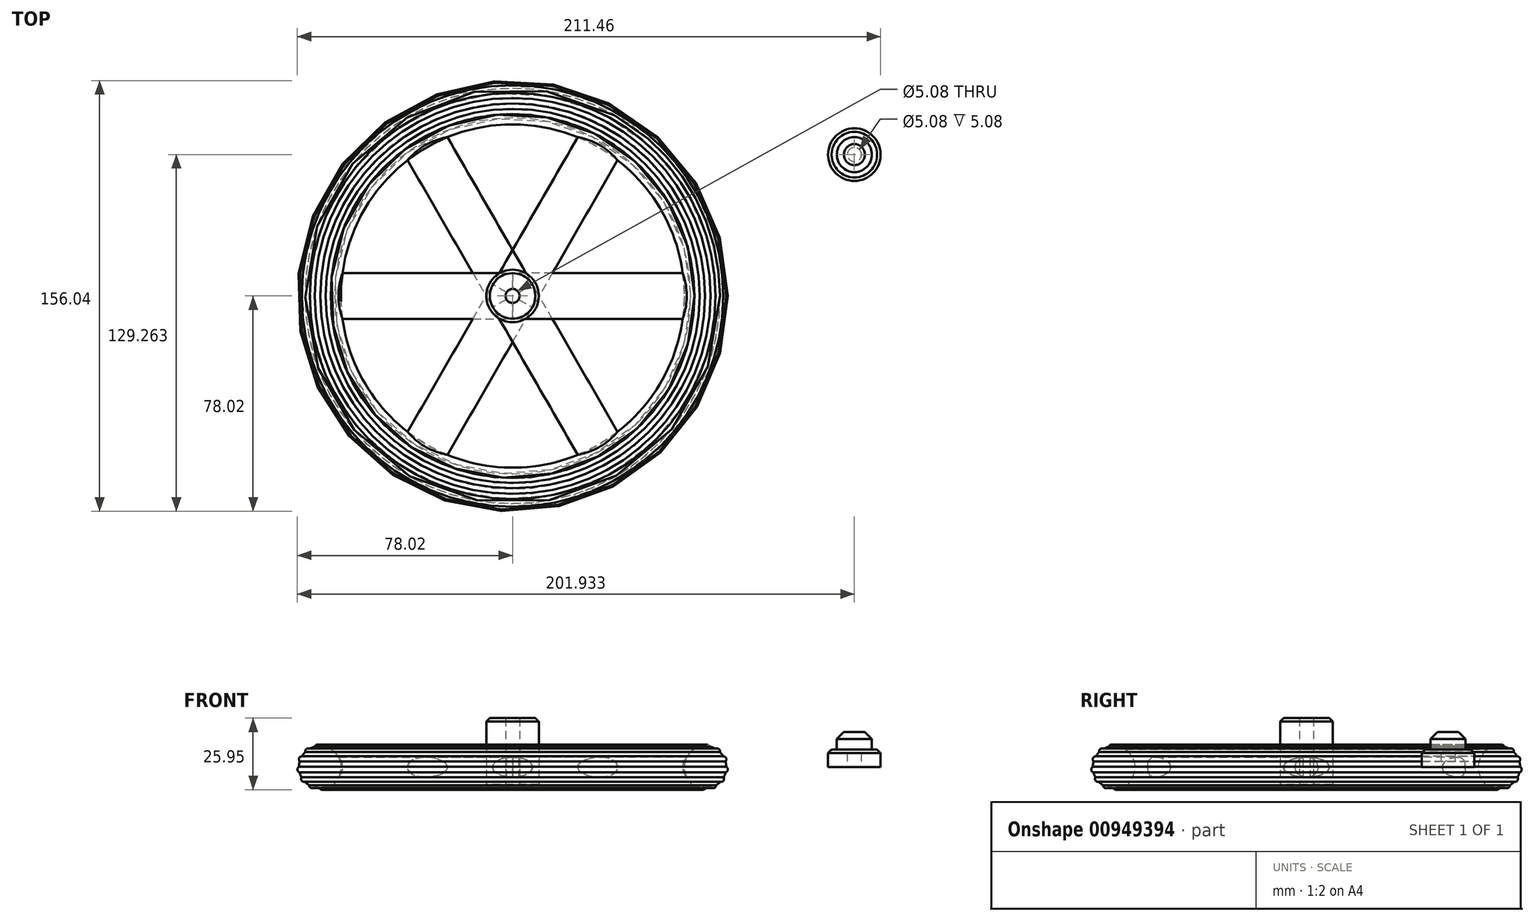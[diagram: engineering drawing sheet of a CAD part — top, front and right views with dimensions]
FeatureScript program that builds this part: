
annotation { "Feature Type Name" : "Feature", "Feature Type Description" : "" }
export const myFeature = defineFeature(function(context is Context, id is Id, definition is map)
    precondition{}
    {
        {
            var Q0;
            Q0=qCreatedBy(makeId("Front.planeOp"),FACE);
            var sketch = newSketch(context, id + "F0", { "sketchPlane" : qUnion([Q0])});
            skArc(sketch, "E0", {"start": v(-71.73, 7.38) * mm, "mid": v(-72.66, 7.08) * mm, "end": v(-73.55, 6.66) * mm});
            skArc(sketch, "E1", {"start": v(-69.72, 7.62) * mm, "mid": v(-70.8, 8.16) * mm, "end": v(-71.73, 7.38) * mm});
            skArc(sketch, "E2.1.1", {"start": v(-73.55, 6.66) * mm, "mid": v(-74.76, 6.6) * mm, "end": v(-75.17, 5.45) * mm});
            skArc(sketch, "E2.2.1", {"start": v(-76.38, 3.92) * mm, "mid": v(-77.4, 3.26) * mm, "end": v(-77.19, 2.06) * mm});
            skArc(sketch, "E2.3.1", {"start": v(-77.47, 0.13) * mm, "mid": v(-78.01, -0.95) * mm, "end": v(-77.23, -1.88) * mm});
            skArc(sketch, "E2.4.1", {"start": v(-76.51, -3.7) * mm, "mid": v(-76.44, -4.9) * mm, "end": v(-75.3, -5.32) * mm});
            skArc(sketch, "E2.5.1", {"start": v(-73.77, -6.53) * mm, "mid": v(-73.1, -7.55) * mm, "end": v(-71.91, -7.34) * mm});
            skArc(sketch, "E2.6.1", {"start": v(-69.98, -7.62) * mm, "mid": v(-68.9, -8.16) * mm, "end": v(-67.97, -7.38) * mm});
            skArc(sketch, "E2.7.1", {"start": v(-66.15, -6.66) * mm, "mid": v(-64.94, -6.6) * mm, "end": v(-64.53, -5.45) * mm});
            skArc(sketch, "E2.11.1", {"start": v(-65.93, 6.53) * mm, "mid": v(-66.6, 7.55) * mm, "end": v(-67.79, 7.34) * mm});
            skArc(sketch, "E3.trimOffspring", {"start": v(-75.17, 5.45) * mm, "mid": v(-75.83, 4.73) * mm, "end": v(-76.38, 3.92) * mm});
            skArc(sketch, "E4.trimOffspring", {"start": v(-67.79, 7.34) * mm, "mid": v(-68.75, 7.54) * mm, "end": v(-69.72, 7.62) * mm});
            skArc(sketch, "E5.trimOffspring", {"start": v(-62.92, 3.16) * mm, "mid": v(-64.17, 5.07) * mm, "end": v(-65.93, 6.53) * mm});
            skArc(sketch, "E6.trimOffspring", {"start": v(-62.36, -1.42) * mm, "mid": v(-62.28, 0.9) * mm, "end": v(-62.9, 3.13) * mm});
            skArc(sketch, "E7.trimOffspring", {"start": v(-64.55, -5.48) * mm, "mid": v(-63.14, -3.6) * mm, "end": v(-62.36, -1.4) * mm});
            skArc(sketch, "E8.trimOffspring", {"start": v(-64.53, -5.45) * mm, "mid": v(-75.16, 5.46) * mm, "end": v(-64.55, -5.47) * mm});
            skArc(sketch, "E9.trimOffspring", {"start": v(-67.97, -7.38) * mm, "mid": v(-67.04, -7.08) * mm, "end": v(-66.15, -6.66) * mm});
            skArc(sketch, "E10.trimOffspring", {"start": v(-71.91, -7.34) * mm, "mid": v(-70.95, -7.54) * mm, "end": v(-69.98, -7.62) * mm});
            skArc(sketch, "E11.trimOffspring", {"start": v(-75.3, -5.32) * mm, "mid": v(-74.58, -5.98) * mm, "end": v(-73.77, -6.53) * mm});
            skArc(sketch, "E12.trimOffspring", {"start": v(-77.23, -1.88) * mm, "mid": v(-76.93, -2.81) * mm, "end": v(-76.51, -3.7) * mm});
            skArc(sketch, "E13.trimOffspring", {"start": v(-77.19, 2.06) * mm, "mid": v(-77.39, 1.1) * mm, "end": v(-77.47, 0.13) * mm});
            skPoint(sketch, "E14", {"position": v(0, 0) * mm});
            skLineSegment(sketch, "E15", {"start": v(0, 13.3) * mm, "end": v(0, -16.91) * mm, "construction": true});
            skLineSegment(sketch, "E16", {"start": v(0, 0) * mm, "end": v(-69.85, 0) * mm, "construction": true});
            skSolve(sketch);
        }
        {
            var Q0;
            Q0=makeQuery(id+"F0.imprint","IMPRINT",FACE,{"disambiguationData":[TD([[makeQuery(id+"F0.imprint","IMPRINT",EDGE,{"derivedFrom":sQuery(id+"F0.wireOp",EDGE,"E0")}),1.0]])]});
            var Q1;
            {var subQ12=sQuery(id+"F0.wireOp",EDGE,"E7.trimOffspring");Q1=makeQuery(id+"F0.imprint","IMPRINT",FACE,{"disambiguationData":[TD([[makeQuery(id+"F0.imprint","IMPRINT",EDGE,{"derivedFrom":subQ12}),1.0]])]});}
            var Q2;
            {var subQ0=sQuery(id+"F0.wireOp",EDGE,"E1");Q2=makeQuery(id+"F0.imprint","IMPRINT",FACE,{"disambiguationData":[TD([[makeQuery(id+"F0.imprint","IMPRINT",EDGE,{"derivedFrom":subQ0}),1.0]])]});}
            var Q3;
            {var subQ0=sQuery(id+"F0.wireOp",EDGE,"E2.1.1");Q3=makeQuery(id+"F0.imprint","IMPRINT",FACE,{"disambiguationData":[TD([[makeQuery(id+"F0.imprint","IMPRINT",EDGE,{"derivedFrom":subQ0}),1.0]])]});}
            var Q4;
            {var subQ0=sQuery(id+"F0.wireOp",EDGE,"E2.2.1");Q4=makeQuery(id+"F0.imprint","IMPRINT",FACE,{"disambiguationData":[TD([[makeQuery(id+"F0.imprint","IMPRINT",EDGE,{"derivedFrom":subQ0}),1.0]])]});}
            var Q5;
            {var subQ0=sQuery(id+"F0.wireOp",EDGE,"E2.3.1");Q5=makeQuery(id+"F0.imprint","IMPRINT",FACE,{"disambiguationData":[TD([[makeQuery(id+"F0.imprint","IMPRINT",EDGE,{"derivedFrom":subQ0}),1.0]])]});}
            var Q6;
            {var subQ0=sQuery(id+"F0.wireOp",EDGE,"E2.4.1");Q6=makeQuery(id+"F0.imprint","IMPRINT",FACE,{"disambiguationData":[TD([[makeQuery(id+"F0.imprint","IMPRINT",EDGE,{"derivedFrom":subQ0}),1.0]])]});}
            var Q7;
            {var subQ0=sQuery(id+"F0.wireOp",EDGE,"E2.5.1");Q7=makeQuery(id+"F0.imprint","IMPRINT",FACE,{"disambiguationData":[TD([[makeQuery(id+"F0.imprint","IMPRINT",EDGE,{"derivedFrom":subQ0}),1.0]])]});}
            var Q8;
            {var subQ0=sQuery(id+"F0.wireOp",EDGE,"E2.6.1");Q8=makeQuery(id+"F0.imprint","IMPRINT",FACE,{"disambiguationData":[TD([[makeQuery(id+"F0.imprint","IMPRINT",EDGE,{"derivedFrom":subQ0}),1.0]])]});}
            var Q9;
            {var subQ0=sQuery(id+"F0.wireOp",EDGE,"E2.7.1");Q9=makeQuery(id+"F0.imprint","IMPRINT",FACE,{"disambiguationData":[TD([[makeQuery(id+"F0.imprint","IMPRINT",EDGE,{"derivedFrom":subQ0}),1.0]])]});}
            var Q10;
            {var subQ0=sQuery(id+"F0.wireOp",EDGE,"E2.11.1");Q10=makeQuery(id+"F0.imprint","IMPRINT",FACE,{"disambiguationData":[TD([[makeQuery(id+"F0.imprint","IMPRINT",EDGE,{"derivedFrom":subQ0}),1.0]])]});}
            var Q11;
            Q11=sQuery(id+"F0.wireOp",EDGE,"E15");
            revolve(context, id + "F1", {"surfaceOperationType" : NewSurfaceOperationType.NEW, "entities" : qUnion([Q0, Q1, Q2, Q3, Q4, Q5, Q6, Q7, Q8, Q9, Q10]), "axis" : qUnion([Q11]), "revolveType" : RevolveType.FULL});
        }
        {
            var Q0;
            Q0=qCreatedBy(makeId("Top.planeOp"),FACE);
            cPlane(context, id + "F2", {"entities" : qUnion([Q0]), "cplaneType" : CPlaneType.OFFSET, "offset" : 7.62 * mm, "oppositeDirection" : true, "width" : 152.4 * mm, "height" : 152.4 * mm});
        }
        {
            var Q0;
            Q0=qCreatedBy(id+"F2.planeOp",FACE);
            var sketch = newSketch(context, id + "F3", { "sketchPlane" : qUnion([Q0])});
            skCircle(sketch, "E17", {"center": v(0, 0) * mm, "radius": 9.53 * mm});
            skSolve(sketch);
        }
        {
            var Q0;
            Q0=makeQuery(id+"F3.imprint","IMPRINT",FACE,{"disambiguationData":[TD([[makeQuery(id+"F3.imprint","IMPRINT",EDGE,{"derivedFrom":sQuery(id+"F3.wireOp",EDGE,"E17")}),1.0]])]});
            extrude(context, id + "F4", {"entities" : qUnion([Q0]), "depth" : 25.4 * mm, "offsetDistance" : 25.4 * mm});
        }
        {
            var Q0;
            Q0=qCreatedBy(makeId("Right.planeOp"),FACE);
            var sketch = newSketch(context, id + "F5", { "sketchPlane" : qUnion([Q0])});
            skEllipse(sketch, "E18", {"center": v(0, 0) * mm, "majorRadius": 8.34 * mm, "minorRadius": 3.64 * mm, "majorAxis": v(-1, 0)});
            skSolve(sketch);
        }
        {
            var Q0;
            Q0=makeQuery(id+"F5.imprint","IMPRINT",FACE,{"disambiguationData":[TD([[makeQuery(id+"F5.imprint","IMPRINT",EDGE,{"derivedFrom":sQuery(id+"F5.wireOp",EDGE,"E18")}),1.0]])]});
            var Q1;
            Q1=makeQuery(id+"F1.opRevolve","SWEPT_BODY",BODY,{"disambiguationData":[OSD([sQuery(id+"F0.wireOp",EDGE,"E0"),sQuery(id+"F0.wireOp",EDGE,"E1"),sQuery(id+"F0.wireOp",EDGE,"E2.1.1"),sQuery(id+"F0.wireOp",EDGE,"E2.2.1"),sQuery(id+"F0.wireOp",EDGE,"E2.3.1"),sQuery(id+"F0.wireOp",EDGE,"E2.4.1"),sQuery(id+"F0.wireOp",EDGE,"E2.5.1"),sQuery(id+"F0.wireOp",EDGE,"E2.6.1"),sQuery(id+"F0.wireOp",EDGE,"E2.7.1"),sQuery(id+"F0.wireOp",EDGE,"E2.8.1"),sQuery(id+"F0.wireOp",EDGE,"E2.9.1"),sQuery(id+"F0.wireOp",EDGE,"E2.10.1"),sQuery(id+"F0.wireOp",EDGE,"E2.11.1"),sQuery(id+"F0.wireOp",EDGE,"E3.trimOffspring"),sQuery(id+"F0.wireOp",EDGE,"E4.trimOffspring"),sQuery(id+"F0.wireOp",EDGE,"E5.trimOffspring"),sQuery(id+"F0.wireOp",EDGE,"E6.trimOffspring"),sQuery(id+"F0.wireOp",EDGE,"E7.trimOffspring"),sQuery(id+"F0.wireOp",EDGE,"E8.trimOffspring"),sQuery(id+"F0.wireOp",EDGE,"E9.trimOffspring"),sQuery(id+"F0.wireOp",EDGE,"E10.trimOffspring"),sQuery(id+"F0.wireOp",EDGE,"E11.trimOffspring"),sQuery(id+"F0.wireOp",EDGE,"E12.trimOffspring"),sQuery(id+"F0.wireOp",EDGE,"E13.trimOffspring")])]});
            extrude(context, id + "F6", {"entities" : qUnion([Q0]), "endBound" : BoundingType.UP_TO_BODY, "depth" : 63.5 * mm, "endBoundEntityBody" : qUnion([Q1]), "offsetDistance" : 25.4 * mm});
        }
        {
            var Q0;
            Q0=makeQuery(id+"F6.opExtrude","SWEPT_BODY",BODY,{"disambiguationData":[OSD([sQuery(id+"F5.wireOp",EDGE,"E18")])]});
            var Q1;
            Q1=makeQuery(id+"F4.opExtrude","SWEPT_FACE",FACE,{"disambiguationData":[OSD([sQuery(id+"F3.wireOp",EDGE,"E17")])]});
            circularPattern(context, id + "F7", {"entities" : qUnion([Q0]), "axis" : qUnion([Q1]), "angle" : 360 * degree, "instanceCount" : 6, "equalSpace" : true});
        }
        {
            var Q0;
            Q0=qCreatedBy(id+"F2.planeOp",FACE);
            var sketch = newSketch(context, id + "F8", { "sketchPlane" : qUnion([Q0])});
            skCircle(sketch, "E19", {"center": v(0, 0) * mm, "radius": 2.54 * mm});
            skSolve(sketch);
        }
        {
            var Q0;
            Q0=makeQuery(id+"F8.imprint","IMPRINT",FACE,{"disambiguationData":[TD([[makeQuery(id+"F8.imprint","IMPRINT",EDGE,{"derivedFrom":sQuery(id+"F8.wireOp",EDGE,"E19")}),1.0]])]});
            extrude(context, id + "F9", {"entities" : qUnion([Q0]), "operationType" : NewBodyOperationType.REMOVE, "endBound" : BoundingType.THROUGH_ALL, "depth" : 38.1 * mm, "offsetDistance" : 25.4 * mm});
        }
        {
            var Q0;
            Q0=makeQuery(id+"F4.opExtrude","CAP_EDGE",EDGE,{"disambiguationData":[OSD([sQuery(id+"F3.wireOp",EDGE,"E17")])],"isStart":true});
            var Q1;
            Q1=makeQuery(id+"F4.opExtrude","CAP_EDGE",EDGE,{"disambiguationData":[OSD([sQuery(id+"F3.wireOp",EDGE,"E17")])],"isStart":false});
            chamfer(context, id + "F10", {"entities" : qUnion([Q0, Q1]), "width" : 1.27 * mm, "tangentPropagation" : true});
        }
        {
            var Q0;
            Q0=qCreatedBy(makeId("Top.planeOp"),FACE);
            var sketch = newSketch(context, id + "F11", { "sketchPlane" : qUnion([Q0])});
            skCircle(sketch, "E20", {"center": v(123.91, 51.24) * mm, "radius": 9.53 * mm});
            skSolve(sketch);
        }
        {
            var Q0;
            Q0=makeQuery(id+"F11.imprint","IMPRINT",FACE,{"disambiguationData":[TD([[makeQuery(id+"F11.imprint","IMPRINT",EDGE,{"derivedFrom":sQuery(id+"F11.wireOp",EDGE,"E20")}),1.0]])]});
            extrude(context, id + "F12", {"entities" : qUnion([Q0]), "depth" : 6.35 * mm, "offsetDistance" : 25.4 * mm});
        }
        {
            var Q0;
            Q0=makeQuery(id+"F12.opExtrude","CAP_FACE",FACE,{"disambiguationData":[OSD([sQuery(id+"F11.wireOp",EDGE,"E20")])],"isStart":false});
            var sketch = newSketch(context, id + "F13", { "sketchPlane" : qUnion([Q0])});
            skCircle(sketch, "E21", {"center": v(123.91, 51.24) * mm, "radius": 6.35 * mm});
            skSolve(sketch);
        }
        {
            var Q0;
            Q0=makeQuery(id+"F13.imprint","IMPRINT",FACE,{"disambiguationData":[TD([[makeQuery(id+"F13.imprint","IMPRINT",EDGE,{"derivedFrom":sQuery(id+"F13.wireOp",EDGE,"E21")}),1.0]])]});
            extrude(context, id + "F14", {"entities" : qUnion([Q0]), "operationType" : NewBodyOperationType.ADD, "depth" : 6.35 * mm, "offsetDistance" : 25.4 * mm});
        }
        {
            var Q0;
            Q0=makeQuery(id+"F14.opExtrude","CAP_EDGE",EDGE,{"disambiguationData":[OSD([sQuery(id+"F13.wireOp",EDGE,"E21")])],"isStart":false});
            chamfer(context, id + "F15", {"entities" : qUnion([Q0]), "width" : 2.54 * mm, "tangentPropagation" : true});
        }
        {
            var Q0;
            Q0=makeQuery(id+"F12.opExtrude","CAP_EDGE",EDGE,{"disambiguationData":[OSD([sQuery(id+"F11.wireOp",EDGE,"E20")])],"isStart":false});
            chamfer(context, id + "F16", {"entities" : qUnion([Q0]), "width" : 1.27 * mm, "tangentPropagation" : true});
        }
        {
            var Q0;
            Q0=makeQuery(id+"F12.opExtrude","CAP_FACE",FACE,{"disambiguationData":[OSD([sQuery(id+"F11.wireOp",EDGE,"E20")])],"isStart":true});
            var sketch = newSketch(context, id + "F17", { "sketchPlane" : qUnion([Q0])});
            skCircle(sketch, "E22", {"center": v(123.91, -51.24) * mm, "radius": 2.54 * mm});
            skSolve(sketch);
        }
        {
            var Q0;
            Q0=makeQuery(id+"F17.imprint","IMPRINT",FACE,{"disambiguationData":[TD([[makeQuery(id+"F17.imprint","IMPRINT",EDGE,{"derivedFrom":sQuery(id+"F17.wireOp",EDGE,"E22")}),1.0]])]});
            extrude(context, id + "F18", {"entities" : qUnion([Q0]), "operationType" : NewBodyOperationType.REMOVE, "oppositeDirection" : true, "depth" : 5.08 * mm, "offsetDistance" : 25.4 * mm});
        }
    });
